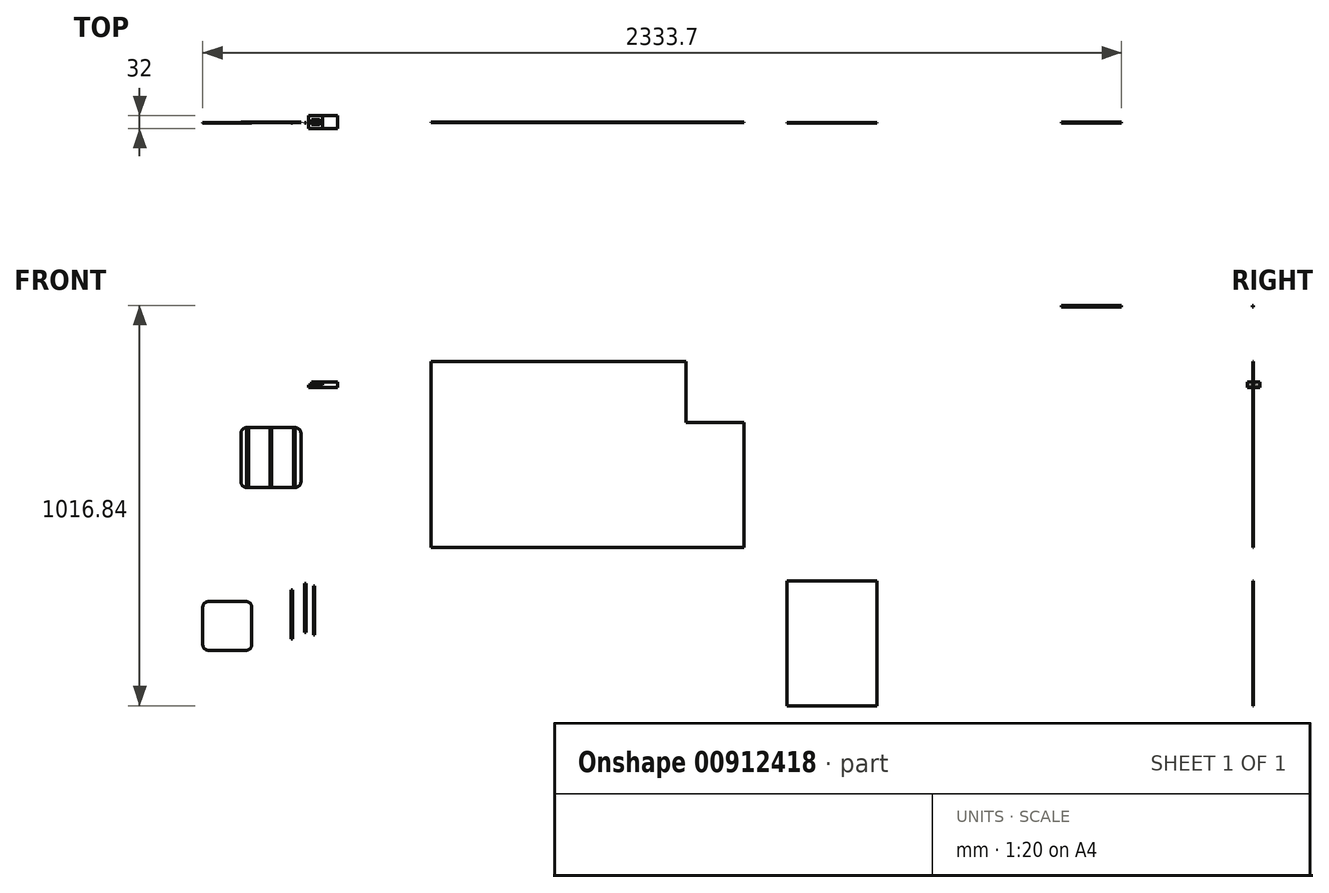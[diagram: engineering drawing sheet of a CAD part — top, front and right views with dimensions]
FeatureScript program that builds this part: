
annotation { "Feature Type Name" : "Feature", "Feature Type Description" : "" }
export const myFeature = defineFeature(function(context is Context, id is Id, definition is map)
    precondition{}
    {
        {
            var Q0;
            Q0=qCreatedBy(makeId("Front.planeOp"),FACE);
            var sketch = newSketch(context, id + "F0", { "sketchPlane" : qUnion([Q0])});
            skLineSegment(sketch, "E0.bottom", {"start": v(766.3, 678.17) * mm, "end": v(888.7, 678.17) * mm});
            skLineSegment(sketch, "E0.top", {"start": v(766.3, 525.77) * mm, "end": v(888.7, 525.77) * mm});
            skLineSegment(sketch, "E0.left", {"start": v(751.3, 663.17) * mm, "end": v(751.3, 540.77) * mm});
            skLineSegment(sketch, "E0.right", {"start": v(903.7, 663.17) * mm, "end": v(903.7, 540.77) * mm});
            skPoint(sketch, "E1.visualSharp", {"position": v(751.3, 678.17) * mm});
            skArc(sketch, "E1.filletArc", {"start": v(766.3, 678.17) * mm, "mid": v(755.7, 673.78) * mm, "end": v(751.3, 663.17) * mm});
            skPoint(sketch, "E2.visualSharp", {"position": v(903.7, 678.17) * mm});
            skArc(sketch, "E2.filletArc", {"start": v(903.7, 663.17) * mm, "mid": v(899.3, 673.78) * mm, "end": v(888.7, 678.17) * mm});
            skPoint(sketch, "E3.visualSharp", {"position": v(903.7, 525.77) * mm});
            skArc(sketch, "E3.filletArc", {"start": v(888.7, 525.77) * mm, "mid": v(899.3, 530.16) * mm, "end": v(903.7, 540.77) * mm});
            skPoint(sketch, "E4.visualSharp", {"position": v(751.3, 525.77) * mm});
            skArc(sketch, "E4.filletArc", {"start": v(751.3, 540.77) * mm, "mid": v(755.7, 530.16) * mm, "end": v(766.3, 525.77) * mm});
            skLineSegment(sketch, "E5.bottom", {"start": v(3038.85, 81858.35) * mm, "end": v(2869.38, 81858.35) * mm});
            skLineSegment(sketch, "E5.top", {"start": v(3038.85, 72650.5) * mm, "end": v(2869.38, 72650.5) * mm});
            skLineSegment(sketch, "E5.left", {"start": v(3038.85, 81858.35) * mm, "end": v(3038.85, 72650.5) * mm});
            skLineSegment(sketch, "E5.right", {"start": v(2869.38, 81858.35) * mm, "end": v(2869.38, 72650.5) * mm});
            skSolve(sketch);
        }
        {
            var Q0;
            Q0=makeQuery(id+"F0.imprint","IMPRINT",FACE,{"disambiguationData":[TD([[makeQuery(id+"F0.imprint","IMPRINT",EDGE,{"derivedFrom":sQuery(id+"F0.wireOp",EDGE,"E0.bottom")}),-1.0]])]});
            extrude(context, id + "F1", {"entities" : qUnion([Q0]), "depth" : 1 * mm, "offsetDistance" : 25 * mm});
        }
        {
            var Q0;
            Q0=makeQuery(id+"F1.opExtrude","CAP_FACE",FACE,{"disambiguationData":[OSD([sQuery(id+"F0.wireOp",EDGE,"E0.bottom"),sQuery(id+"F0.wireOp",EDGE,"E0.top"),sQuery(id+"F0.wireOp",EDGE,"E0.left"),sQuery(id+"F0.wireOp",EDGE,"E0.right"),sQuery(id+"F0.wireOp",EDGE,"E1.filletArc"),sQuery(id+"F0.wireOp",EDGE,"E2.filletArc"),sQuery(id+"F0.wireOp",EDGE,"E3.filletArc"),sQuery(id+"F0.wireOp",EDGE,"E4.filletArc")])],"isStart":false});
            var sketch = newSketch(context, id + "F2", { "sketchPlane" : qUnion([Q0])});
            skLineSegment(sketch, "E6.bottom", {"start": v(1067.58, 689.47) * mm, "end": v(1071.78, 689.47) * mm});
            skLineSegment(sketch, "E6.top", {"start": v(1067.58, 537.07) * mm, "end": v(1071.78, 537.07) * mm});
            skLineSegment(sketch, "E6.left", {"start": v(1067.58, 689.47) * mm, "end": v(1067.58, 537.07) * mm});
            skLineSegment(sketch, "E6.right", {"start": v(1071.78, 689.47) * mm, "end": v(1071.78, 537.07) * mm});
            skLineSegment(sketch, "E7.bottom", {"start": v(1040.2, 697.09) * mm, "end": v(1044.38, 697.09) * mm});
            skLineSegment(sketch, "E7.top", {"start": v(1040.2, 544.69) * mm, "end": v(1044.38, 544.69) * mm});
            skLineSegment(sketch, "E7.left", {"start": v(1040.2, 697.09) * mm, "end": v(1040.2, 544.69) * mm});
            skLineSegment(sketch, "E7.right", {"start": v(1044.38, 697.09) * mm, "end": v(1044.38, 544.69) * mm});
            skLineSegment(sketch, "E8.bottom", {"start": v(998.8, 676.8) * mm, "end": v(1003, 676.8) * mm});
            skLineSegment(sketch, "E8.top", {"start": v(998.8, 524.4) * mm, "end": v(1003, 524.4) * mm});
            skLineSegment(sketch, "E8.left", {"start": v(998.8, 676.8) * mm, "end": v(998.8, 524.4) * mm});
            skLineSegment(sketch, "E8.right", {"start": v(1003, 676.8) * mm, "end": v(1003, 524.4) * mm});
            skSolve(sketch);
        }
        {
            var Q0;
            Q0=makeQuery(id+"F2.imprint","IMPRINT",FACE,{"disambiguationData":[TD([[makeQuery(id+"F2.imprint","IMPRINT",EDGE,{"derivedFrom":sQuery(id+"F2.wireOp",EDGE,"E6.bottom")}),-1.0]])]});
            var Q1;
            Q1=makeQuery(id+"F2.imprint","IMPRINT",FACE,{"disambiguationData":[TD([[makeQuery(id+"F2.imprint","IMPRINT",EDGE,{"derivedFrom":sQuery(id+"F2.wireOp",EDGE,"E7.bottom")}),-1.0]])]});
            var Q2;
            Q2=makeQuery(id+"F2.imprint","IMPRINT",FACE,{"disambiguationData":[TD([[makeQuery(id+"F2.imprint","IMPRINT",EDGE,{"derivedFrom":sQuery(id+"F2.wireOp",EDGE,"E8.bottom")}),-1.0]])]});
            extrude(context, id + "F3", {"entities" : qUnion([Q0, Q1, Q2]), "depth" : 0.5 * mm, "offsetDistance" : 25 * mm});
        }
        {
            var Q0;
            Q0=makeQuery(id+"F3.opExtrude","SWEPT_BODY",BODY,{"disambiguationData":[OSD([sQuery(id+"F2.wireOp",EDGE,"E8.bottom"),sQuery(id+"F2.wireOp",EDGE,"E8.top"),sQuery(id+"F2.wireOp",EDGE,"E8.left"),sQuery(id+"F2.wireOp",EDGE,"E8.right")])]});
            transform(context, id + "F4", {"entities" : qUnion([Q0]), "transformType" : TransformType.TRANSLATION_3D, "dx" : -232.8 * mm, "dy" : 0 * mm, "dz" : 3.3 * mm, "makeCopy" : false});
        }
        {
            var Q0;
            Q0=makeQuery(id+"F3.opExtrude","SWEPT_BODY",BODY,{"disambiguationData":[OSD([sQuery(id+"F2.wireOp",EDGE,"E8.bottom"),sQuery(id+"F2.wireOp",EDGE,"E8.top"),sQuery(id+"F2.wireOp",EDGE,"E8.left"),sQuery(id+"F2.wireOp",EDGE,"E8.right")])]});
            transform(context, id + "F5", {"entities" : qUnion([Q0]), "transformType" : TransformType.TRANSLATION_3D, "dx" : 6E-4000 * mm, "dy" : 0 * mm, "dz" : 0 * mm, "makeCopy" : false});
        }
        {
            var Q0;
            Q0=makeQuery(id+"F3.opExtrude","SWEPT_BODY",BODY,{"disambiguationData":[OSD([sQuery(id+"F2.wireOp",EDGE,"E8.bottom"),sQuery(id+"F2.wireOp",EDGE,"E8.top"),sQuery(id+"F2.wireOp",EDGE,"E8.left"),sQuery(id+"F2.wireOp",EDGE,"E8.right")])]});
            var Q1;
            Q1=makeQuery(id+"F3.opExtrude","CAP_VERTEX",VERTEX,{"disambiguationData":[OSD([sQuery(id+"F2.wireOp",EDGE,"E8.top"),sQuery(id+"F2.wireOp",EDGE,"E8.left")])],"isStart":false});
            var Q2;
            Q2=makeQuery(id+"F1.opExtrude","CAP_EDGE",EDGE,{"disambiguationData":[OSD([sQuery(id+"F0.wireOp",EDGE,"E0.top")])],"isStart":false});
            transform(context, id + "F6", {"entities" : qUnion([Q0]), "transformType" : TransformType.TRANSLATION_ENTITY, "oppositeDirectionEntity" : false, "transformLine" : qUnion([Q1, Q2]), "makeCopy" : false});
        }
        {
            var Q0;
            Q0=makeQuery(id+"F3.opExtrude","SWEPT_BODY",BODY,{"disambiguationData":[OSD([sQuery(id+"F2.wireOp",EDGE,"E8.bottom"),sQuery(id+"F2.wireOp",EDGE,"E8.top"),sQuery(id+"F2.wireOp",EDGE,"E8.left"),sQuery(id+"F2.wireOp",EDGE,"E8.right")])]});
            var Q1;
            Q1=makeQuery(id+"F3.opExtrude","CAP_VERTEX",VERTEX,{"disambiguationData":[OSD([sQuery(id+"F2.wireOp",EDGE,"E8.bottom"),sQuery(id+"F2.wireOp",EDGE,"E8.right")])],"isStart":true});
            var Q2;
            Q2=makeQuery(id+"F1.opExtrude","CAP_VERTEX",VERTEX,{"disambiguationData":[OSD([sQuery(id+"F0.wireOp",EDGE,"E0.bottom"),sQuery(id+"F0.wireOp",EDGE,"E2.filletArc")])],"isStart":false});
            transform(context, id + "F7", {"entities" : qUnion([Q0]), "transformType" : TransformType.TRANSLATION_ENTITY, "oppositeDirectionEntity" : false, "transformLine" : qUnion([Q1, Q2]), "makeCopy" : false});
        }
        {
            var Q0;
            Q0=makeQuery(id+"F3.opExtrude","SWEPT_BODY",BODY,{"disambiguationData":[OSD([sQuery(id+"F2.wireOp",EDGE,"E7.bottom"),sQuery(id+"F2.wireOp",EDGE,"E7.top"),sQuery(id+"F2.wireOp",EDGE,"E7.left"),sQuery(id+"F2.wireOp",EDGE,"E7.right")])]});
            var Q1;
            Q1=sQuery(id+"F2.wireOp",VERTEX,"E7.bottom.start");
            var Q2;
            Q2=makeQuery(id+"F1.opExtrude","CAP_VERTEX",VERTEX,{"disambiguationData":[OSD([sQuery(id+"F0.wireOp",EDGE,"E0.bottom"),sQuery(id+"F0.wireOp",EDGE,"E1.filletArc")])],"isStart":false});
            transform(context, id + "F8", {"entities" : qUnion([Q0]), "transformType" : TransformType.TRANSLATION_ENTITY, "oppositeDirectionEntity" : false, "transformLine" : qUnion([Q1, Q2]), "makeCopy" : false});
        }
        {
            var Q0;
            Q0=sQuery(id+"F2.wireOp",EDGE,"E6.bottom");
            cPoint(context, id + "F9", {"entities" : qUnion([Q0]), "parameter" : 0.5});
        }
        {
            var Q0;
            Q0=makeQuery(id+"F1.opExtrude","CAP_EDGE",EDGE,{"disambiguationData":[OSD([sQuery(id+"F0.wireOp",EDGE,"E0.bottom")])],"isStart":false});
            cPoint(context, id + "F10", {"entities" : qUnion([Q0]), "parameter" : 0.5});
        }
        {
            var Q0;
            Q0=makeQuery(id+"F3.opExtrude","SWEPT_BODY",BODY,{"disambiguationData":[OSD([sQuery(id+"F2.wireOp",EDGE,"E6.bottom"),sQuery(id+"F2.wireOp",EDGE,"E6.top"),sQuery(id+"F2.wireOp",EDGE,"E6.left"),sQuery(id+"F2.wireOp",EDGE,"E6.right")])]});
            var Q1;
            Q1=qCreatedBy(id+"F9",VERTEX);
            var Q2;
            Q2=qCreatedBy(id+"F10",VERTEX);
            transform(context, id + "F11", {"entities" : qUnion([Q0]), "transformType" : TransformType.TRANSLATION_ENTITY, "oppositeDirectionEntity" : false, "transformLine" : qUnion([Q1, Q2]), "makeCopy" : false});
        }
        {
            var Q0;
            Q0=qCreatedBy(makeId("Front.planeOp"),FACE);
            var sketch = newSketch(context, id + "F12", { "sketchPlane" : qUnion([Q0])});
            skLineSegment(sketch, "E9.right", {"start": v(997.16, 786.05) * mm, "end": v(997.16, 780.2) * mm});
            skPoint(sketch, "E10.oppositeSnap0", {"position": v(958.16, 786.05) * mm});
            skLineSegment(sketch, "E10.bottom", {"start": v(997.16, 786.05) * mm, "end": v(958.16, 786.05) * mm});
            skLineSegment(sketch, "E10.top", {"start": v(997.16, 794.2) * mm, "end": v(958.16, 794.2) * mm});
            skLineSegment(sketch, "E10.left", {"start": v(997.16, 786.05) * mm, "end": v(997.16, 794.2) * mm});
            skLineSegment(sketch, "E10.right", {"start": v(958.16, 786.05) * mm, "end": v(958.16, 794.2) * mm});
            skLineSegment(sketch, "E11.bottom", {"start": v(958.16, 790.13) * mm, "end": v(930.77, 790.13) * mm});
            skLineSegment(sketch, "E11.top", {"start": v(958.16, 786.05) * mm, "end": v(930.77, 786.05) * mm});
            skLineSegment(sketch, "E11.left", {"start": v(958.16, 790.13) * mm, "end": v(958.16, 786.05) * mm});
            skLineSegment(sketch, "E11.right", {"start": v(930.77, 790.13) * mm, "end": v(930.77, 786.05) * mm});
            skLineSegment(sketch, "E12", {"start": v(997.16, 780.2) * mm, "end": v(923.16, 780.2) * mm});
            skLineSegment(sketch, "E13", {"start": v(923.16, 780.2) * mm, "end": v(923.16, 786.05) * mm});
            skLineSegment(sketch, "E14", {"start": v(923.16, 786.05) * mm, "end": v(930.77, 786.05) * mm});
            skSolve(sketch);
        }
        {
            var Q0;
            Q0=makeQuery(id+"F12.imprint","IMPRINT",FACE,{"disambiguationData":[TD([[makeQuery(id+"F12.imprint","IMPRINT",EDGE,{"derivedFrom":sQuery(id+"F12.wireOp",EDGE,"E10.bottom")}),-1.0]])]});
            var Q1;
            Q1=makeQuery(id+"F12.imprint","IMPRINT",FACE,{"disambiguationData":[TD([[makeQuery(id+"F12.imprint","IMPRINT",EDGE,{"derivedFrom":sQuery(id+"F12.wireOp",EDGE,"E9.bottom")}),-1.0]])]});
            var Q2;
            Q2=makeQuery(id+"F12.imprint","IMPRINT",FACE,{"disambiguationData":[TD([[makeQuery(id+"F12.imprint","IMPRINT",EDGE,{"derivedFrom":sQuery(id+"F12.wireOp",EDGE,"E9.right")}),-1.0]])]});
            extrude(context, id + "F13", {"entities" : qUnion([Q0, Q1, Q2]), "endBound" : BoundingType.SYMMETRIC, "depth" : 32 * mm, "offsetDistance" : 25 * mm});
        }
        {
            var Q0;
            Q0=makeQuery(id+"F12.imprint","IMPRINT",FACE,{"disambiguationData":[TD([[makeQuery(id+"F12.imprint","IMPRINT",EDGE,{"derivedFrom":sQuery(id+"F12.wireOp",EDGE,"E11.bottom")}),1.0]])]});
            var Q1;
            Q1=sQuery(id+"F12.wireOp",EDGE,"E11.bottom");
            revolve(context, id + "F14", {"surfaceOperationType" : NewSurfaceOperationType.NEW, "entities" : qUnion([Q0]), "axis" : qUnion([Q1]), "revolveType" : RevolveType.ONE_DIRECTION, "angle" : 360 * degree});
        }
        {
            var Q0;
            Q0=makeQuery(id+"F14.opRevolve","SWEPT_FACE",FACE,{"disambiguationData":[OSD([sQuery(id+"F12.wireOp",EDGE,"E11.right")])]});
            var sketch = newSketch(context, id + "F15", { "sketchPlane" : qUnion([Q0])});
            skCircle(sketch, "E15", {"center": v(0, 790.13) * mm, "radius": 7.66 * mm});
            skSolve(sketch);
        }
        {
            var Q0;
            Q0=makeQuery(id+"F15.imprint","IMPRINT",FACE,{"disambiguationData":[TD([[makeQuery(id+"F15.imprint","IMPRINT",EDGE,{"derivedFrom":sQuery(id+"F15.wireOp",EDGE,"E15")}),1.0]])]});
            extrude(context, id + "F16", {"entities" : qUnion([Q0]), "operationType" : NewBodyOperationType.REMOVE, "depth" : -20 * mm, "offsetDistance" : 25 * mm});
        }
        {
            var Q0;
            Q0=makeQuery(id+"F1.opExtrude","CAP_FACE",FACE,{"disambiguationData":[OSD([sQuery(id+"F0.wireOp",EDGE,"E0.bottom"),sQuery(id+"F0.wireOp",EDGE,"E0.top"),sQuery(id+"F0.wireOp",EDGE,"E0.left"),sQuery(id+"F0.wireOp",EDGE,"E0.right"),sQuery(id+"F0.wireOp",EDGE,"E1.filletArc"),sQuery(id+"F0.wireOp",EDGE,"E2.filletArc"),sQuery(id+"F0.wireOp",EDGE,"E3.filletArc"),sQuery(id+"F0.wireOp",EDGE,"E4.filletArc")])],"isStart":false});
            var sketch = newSketch(context, id + "F17", { "sketchPlane" : qUnion([Q0])});
            skLineSegment(sketch, "E16.bottom", {"start": v(1234.72, 846.32) * mm, "end": v(1882.42, 846.32) * mm});
            skLineSegment(sketch, "E16.top", {"start": v(1234.72, 373.88) * mm, "end": v(1882.42, 373.88) * mm});
            skLineSegment(sketch, "E16.left", {"start": v(1234.72, 846.32) * mm, "end": v(1234.72, 373.88) * mm});
            skLineSegment(sketch, "E16.right", {"start": v(1882.42, 846.32) * mm, "end": v(1882.42, 373.88) * mm});
            skLineSegment(sketch, "E17.bottom", {"start": v(1882.42, 373.88) * mm, "end": v(2029.74, 373.88) * mm});
            skLineSegment(sketch, "E17.top", {"start": v(1882.42, 691.38) * mm, "end": v(2029.74, 691.38) * mm});
            skLineSegment(sketch, "E17.left", {"start": v(1882.42, 373.88) * mm, "end": v(1882.42, 691.38) * mm});
            skLineSegment(sketch, "E17.right", {"start": v(2029.74, 373.88) * mm, "end": v(2029.74, 691.38) * mm});
            skSolve(sketch);
        }
        {
            var Q0;
            Q0=makeQuery(id+"F17.imprint","IMPRINT",FACE,{"disambiguationData":[TD([[makeQuery(id+"F17.imprint","IMPRINT",EDGE,{"derivedFrom":sQuery(id+"F17.wireOp",EDGE,"E16.bottom")}),-1.0]])]});
            var Q1;
            Q1=makeQuery(id+"F17.imprint","IMPRINT",FACE,{"disambiguationData":[TD([[makeQuery(id+"F17.imprint","IMPRINT",EDGE,{"derivedFrom":sQuery(id+"F17.wireOp",EDGE,"E17.bottom")}),1.0]])]});
            extrude(context, id + "F18", {"entities" : qUnion([Q0, Q1]), "endBound" : BoundingType.SYMMETRIC, "depth" : 1 * mm, "offsetDistance" : 25.4 * mm});
        }
        {
            var Q0;
            Q0=makeQuery(id+"F18.opExtrude","CAP_FACE",FACE,{"disambiguationData":[OSD([sQuery(id+"F17.wireOp",EDGE,"E16.bottom"),sQuery(id+"F17.wireOp",EDGE,"E16.top"),sQuery(id+"F17.wireOp",EDGE,"E16.left"),sQuery(id+"F17.wireOp",EDGE,"E16.right")])],"isStart":false});
            var sketch = newSketch(context, id + "F19", { "sketchPlane" : qUnion([Q0])});
            skLineSegment(sketch, "E18.bottom", {"start": v(2175.25, 988.19) * mm, "end": v(2988.05, 988.19) * mm});
            skLineSegment(sketch, "E18.top", {"start": v(2175.25, 505.59) * mm, "end": v(2988.05, 505.59) * mm});
            skLineSegment(sketch, "E18.left", {"start": v(2175.25, 988.19) * mm, "end": v(2175.25, 505.59) * mm});
            skLineSegment(sketch, "E18.right", {"start": v(2988.05, 988.19) * mm, "end": v(2988.05, 505.59) * mm});
            skLineSegment(sketch, "E19.bottom", {"start": v(2988.05, 988.19) * mm, "end": v(2835.65, 988.19) * mm});
            skLineSegment(sketch, "E19.top", {"start": v(2988.05, 835.79) * mm, "end": v(2835.65, 835.79) * mm});
            skLineSegment(sketch, "E19.left", {"start": v(2988.05, 988.19) * mm, "end": v(2988.05, 835.79) * mm});
            skLineSegment(sketch, "E19.right", {"start": v(2835.65, 988.19) * mm, "end": v(2835.65, 835.79) * mm});
            skLineSegment(sketch, "E20.bottom", {"start": v(2988.05, 835.79) * mm, "end": v(2984.25, 835.79) * mm});
            skLineSegment(sketch, "E20.top", {"start": v(2988.05, 988.19) * mm, "end": v(2984.25, 988.19) * mm});
            skLineSegment(sketch, "E20.left", {"start": v(2988.05, 835.79) * mm, "end": v(2988.05, 988.19) * mm});
            skLineSegment(sketch, "E20.right", {"start": v(2984.25, 835.79) * mm, "end": v(2984.25, 988.19) * mm});
            skLineSegment(sketch, "E21.bottom", {"start": v(2835.65, 988.19) * mm, "end": v(2988.05, 988.19) * mm});
            skLineSegment(sketch, "E21.top", {"start": v(2835.65, 984.43) * mm, "end": v(2988.05, 984.43) * mm});
            skLineSegment(sketch, "E21.left", {"start": v(2835.65, 988.19) * mm, "end": v(2835.65, 984.43) * mm});
            skLineSegment(sketch, "E21.right", {"start": v(2988.05, 988.19) * mm, "end": v(2988.05, 984.43) * mm});
            skLineSegment(sketch, "E22.bottom", {"start": v(2864.22, 784.99) * mm, "end": v(2908.67, 784.99) * mm});
            skLineSegment(sketch, "E22.top", {"start": v(2864.22, 689.74) * mm, "end": v(2908.67, 689.74) * mm});
            skLineSegment(sketch, "E22.left", {"start": v(2864.22, 784.99) * mm, "end": v(2864.22, 689.74) * mm});
            skLineSegment(sketch, "E22.right", {"start": v(2908.67, 784.99) * mm, "end": v(2908.67, 689.74) * mm});
            skLineSegment(sketch, "E23.bottom", {"start": v(2864.22, 657.99) * mm, "end": v(2908.67, 657.99) * mm});
            skLineSegment(sketch, "E23.top", {"start": v(2864.22, 562.74) * mm, "end": v(2908.67, 562.74) * mm});
            skLineSegment(sketch, "E23.left", {"start": v(2864.22, 657.99) * mm, "end": v(2864.22, 562.74) * mm});
            skLineSegment(sketch, "E23.right", {"start": v(2908.67, 657.99) * mm, "end": v(2908.67, 562.74) * mm});
            skSolve(sketch);
        }
        {
            var Q0;
            Q0=makeQuery(id+"F19.imprint","IMPRINT",FACE,{"disambiguationData":[TD([[makeQuery(id+"F19.imprint","IMPRINT",EDGE,{"derivedFrom":sQuery(id+"F19.wireOp",EDGE,"E18.bottom")}),-1.0]])]});
            var Q1;
            {var subQ5=sQuery(id+"F19.wireOp",EDGE,"E21.left");Q1=makeQuery(id+"F19.imprint","IMPRINT",FACE,{"disambiguationData":[TD([[makeQuery(id+"F19.imprint","IMPRINT",EDGE,{"derivedFrom":subQ5}),1.0]])]});}
            var Q2;
            {var subQ5=sQuery(id+"F19.wireOp",EDGE,"E21.right");Q2=makeQuery(id+"F19.imprint","IMPRINT",FACE,{"disambiguationData":[TD([[makeQuery(id+"F19.imprint","IMPRINT",EDGE,{"derivedFrom":subQ5}),-1.0]])]});}
            var Q3;
            {var subQ0=sQuery(id+"F19.wireOp",EDGE,"E20.bottom");Q3=makeQuery(id+"F19.imprint","IMPRINT",FACE,{"disambiguationData":[TD([[makeQuery(id+"F19.imprint","IMPRINT",EDGE,{"derivedFrom":subQ0}),-1.0]])]});}
            extrude(context, id + "F20", {"entities" : qUnion([Q0, Q1, Q2, Q3]), "endBound" : BoundingType.SYMMETRIC, "depth" : 2.66 * mm, "offsetDistance" : 25.4 * mm});
        }
        {
            var Q0;
            Q0=makeQuery(id+"F18.opExtrude","CAP_FACE",FACE,{"disambiguationData":[OSD([sQuery(id+"F17.wireOp",EDGE,"E16.bottom"),sQuery(id+"F17.wireOp",EDGE,"E16.top"),sQuery(id+"F17.wireOp",EDGE,"E16.left"),sQuery(id+"F17.wireOp",EDGE,"E16.right")])],"isStart":false});
            var sketch = newSketch(context, id + "F21", { "sketchPlane" : qUnion([Q0])});
            skLineSegment(sketch, "E24.bottom", {"start": v(2138.3, 288.85) * mm, "end": v(2366.9, 288.85) * mm});
            skLineSegment(sketch, "E24.top", {"start": v(2138.3, -28.65) * mm, "end": v(2366.9, -28.65) * mm});
            skLineSegment(sketch, "E24.left", {"start": v(2138.3, 288.85) * mm, "end": v(2138.3, -28.65) * mm});
            skLineSegment(sketch, "E24.right", {"start": v(2366.9, 288.85) * mm, "end": v(2366.9, -28.65) * mm});
            skSolve(sketch);
        }
        {
            var Q0;
            Q0=makeQuery(id+"F21.imprint","IMPRINT",FACE,{"disambiguationData":[TD([[makeQuery(id+"F21.imprint","IMPRINT",EDGE,{"derivedFrom":sQuery(id+"F21.wireOp",EDGE,"E24.bottom")}),-1.0]])]});
            extrude(context, id + "F22", {"entities" : qUnion([Q0]), "endBound" : BoundingType.SYMMETRIC, "depth" : 1 * mm, "offsetDistance" : 25.4 * mm});
        }
        {
            var Q0;
            Q0=makeQuery(id+"F18.opExtrude","CAP_FACE",FACE,{"disambiguationData":[OSD([sQuery(id+"F17.wireOp",EDGE,"E16.bottom"),sQuery(id+"F17.wireOp",EDGE,"E16.top"),sQuery(id+"F17.wireOp",EDGE,"E16.left"),sQuery(id+"F17.wireOp",EDGE,"E16.right"),sQuery(id+"F17.wireOp",EDGE,"E17.bottom"),sQuery(id+"F17.wireOp",EDGE,"E17.top"),sQuery(id+"F17.wireOp",EDGE,"E17.right")])],"isStart":false});
            var sketch = newSketch(context, id + "F23", { "sketchPlane" : qUnion([Q0])});
            skLineSegment(sketch, "E25.bottom", {"start": v(669.35, 236.26) * mm, "end": v(763.8, 236.26) * mm});
            skLineSegment(sketch, "E25.top", {"start": v(669.35, 111.8) * mm, "end": v(763.8, 111.8) * mm});
            skLineSegment(sketch, "E25.left", {"start": v(654.35, 221.26) * mm, "end": v(654.35, 126.8) * mm});
            skLineSegment(sketch, "E25.right", {"start": v(778.8, 221.26) * mm, "end": v(778.8, 126.8) * mm});
            skPoint(sketch, "E26.visualSharp", {"position": v(654.35, 236.26) * mm});
            skArc(sketch, "E26.filletArc", {"start": v(669.35, 236.26) * mm, "mid": v(658.74, 231.87) * mm, "end": v(654.35, 221.26) * mm});
            skPoint(sketch, "E27.visualSharp", {"position": v(778.8, 236.26) * mm});
            skArc(sketch, "E27.filletArc", {"start": v(778.8, 221.26) * mm, "mid": v(774.41, 231.87) * mm, "end": v(763.8, 236.26) * mm});
            skPoint(sketch, "E28.visualSharp", {"position": v(778.8, 111.8) * mm});
            skArc(sketch, "E28.filletArc", {"start": v(763.8, 111.8) * mm, "mid": v(774.41, 116.2) * mm, "end": v(778.8, 126.8) * mm});
            skPoint(sketch, "E29.visualSharp", {"position": v(654.35, 111.8) * mm});
            skArc(sketch, "E29.filletArc", {"start": v(654.35, 126.8) * mm, "mid": v(658.74, 116.2) * mm, "end": v(669.35, 111.8) * mm});
            skSolve(sketch);
        }
        {
            var Q0;
            Q0=makeQuery(id+"F23.imprint","IMPRINT",FACE,{"disambiguationData":[TD([[makeQuery(id+"F23.imprint","IMPRINT",EDGE,{"derivedFrom":makeQuery(id+"F18.opExtrude","CAP_EDGE",EDGE,{"disambiguationData":[OSD([sQuery(id+"F17.wireOp",EDGE,"E16.bottom")])],"isStart":false})}),-1.0]])]});
            var sketch = newSketch(context, id + "F24", { "sketchPlane" : qUnion([Q0])});
            skLineSegment(sketch, "E30.bottom", {"start": v(935.57, 276.25) * mm, "end": v(939, 276.25) * mm});
            skLineSegment(sketch, "E30.top", {"start": v(935.57, 151.79) * mm, "end": v(939, 151.79) * mm});
            skLineSegment(sketch, "E30.left", {"start": v(935.57, 276.25) * mm, "end": v(935.57, 151.79) * mm});
            skLineSegment(sketch, "E30.right", {"start": v(939, 276.25) * mm, "end": v(939, 151.79) * mm});
            skLineSegment(sketch, "E31.bottom", {"start": v(913.2, 282.47) * mm, "end": v(916.62, 282.47) * mm});
            skLineSegment(sketch, "E31.top", {"start": v(913.2, 158) * mm, "end": v(916.62, 158) * mm});
            skLineSegment(sketch, "E31.left", {"start": v(913.2, 282.47) * mm, "end": v(913.2, 158) * mm});
            skLineSegment(sketch, "E31.right", {"start": v(916.62, 282.47) * mm, "end": v(916.62, 158) * mm});
            skLineSegment(sketch, "E32.bottom", {"start": v(879.4, 265.9) * mm, "end": v(882.82, 265.9) * mm});
            skLineSegment(sketch, "E32.top", {"start": v(879.4, 141.45) * mm, "end": v(882.82, 141.45) * mm});
            skLineSegment(sketch, "E32.left", {"start": v(879.4, 265.9) * mm, "end": v(879.4, 141.45) * mm});
            skLineSegment(sketch, "E32.right", {"start": v(882.82, 265.9) * mm, "end": v(882.82, 141.45) * mm});
            skSolve(sketch);
        }
        {
            var Q0;
            Q0=makeQuery(id+"F23.imprint","IMPRINT",FACE,{"disambiguationData":[TD([[makeQuery(id+"F23.imprint","IMPRINT",EDGE,{"derivedFrom":sQuery(id+"F23.wireOp",EDGE,"E25.bottom")}),-1.0]])]});
            extrude(context, id + "F25", {"entities" : qUnion([Q0]), "depth" : 0.5 * mm, "offsetDistance" : 25.4 * mm});
        }
        {
            var Q0;
            Q0=makeQuery(id+"F24.imprint","IMPRINT",FACE,{"disambiguationData":[TD([[makeQuery(id+"F24.imprint","IMPRINT",EDGE,{"derivedFrom":sQuery(id+"F24.wireOp",EDGE,"E32.bottom")}),-1.0]])]});
            var Q1;
            Q1=makeQuery(id+"F24.imprint","IMPRINT",FACE,{"disambiguationData":[TD([[makeQuery(id+"F24.imprint","IMPRINT",EDGE,{"derivedFrom":sQuery(id+"F24.wireOp",EDGE,"E31.bottom")}),-1.0]])]});
            var Q2;
            Q2=makeQuery(id+"F24.imprint","IMPRINT",FACE,{"disambiguationData":[TD([[makeQuery(id+"F24.imprint","IMPRINT",EDGE,{"derivedFrom":sQuery(id+"F24.wireOp",EDGE,"E30.bottom")}),-1.0]])]});
            extrude(context, id + "F26", {"entities" : qUnion([Q0, Q1, Q2]), "depth" : 0.5 * mm, "offsetDistance" : 25.4 * mm});
        }
    });
